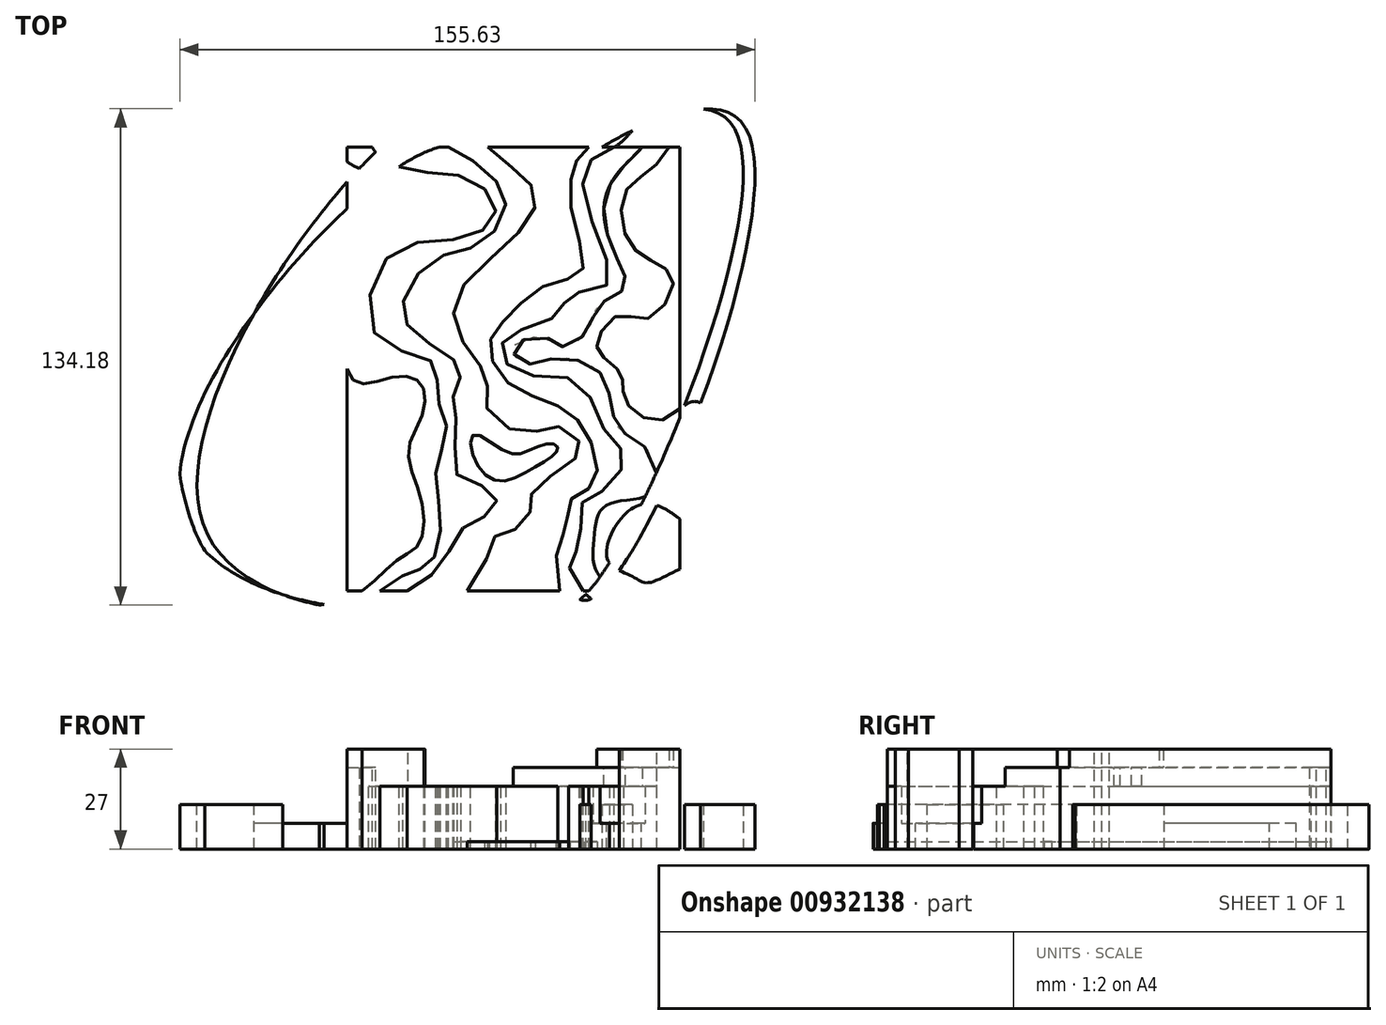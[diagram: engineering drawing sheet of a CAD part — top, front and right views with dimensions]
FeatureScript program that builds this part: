
annotation { "Feature Type Name" : "Feature", "Feature Type Description" : "" }
export const myFeature = defineFeature(function(context is Context, id is Id, definition is map)
    precondition{}
    {
        {
            var Q0;
            Q0=qCreatedBy(makeId("Top.planeOp"),FACE);
            var sketch = newSketch(context, id + "F0", { "sketchPlane" : qUnion([Q0])});
            skLineSegment(sketch, "E0.bottom", {"start": v(-45, 60) * mm, "end": v(-6.97, 60) * mm});
            skLineSegment(sketch, "E0.top", {"start": v(-45, -60) * mm, "end": v(-12.44, -60) * mm});
            skLineSegment(sketch, "E0.left", {"start": v(-45, 60) * mm, "end": v(-45, -60) * mm});
            skLineSegment(sketch, "E0.right", {"start": v(45, 60) * mm, "end": v(45, -60) * mm});
            skPoint(sketch, "E0.middle", {"position": v(0, 0) * mm});
            skLineSegment(sketch, "E1", {"start": v(-6.97, 60) * mm, "end": v(20.41, 60) * mm});
            skFitSpline(sketch, "E2", {"points": [v(16.04, -63.26) * mm, v(11.9, -48.78) * mm, v(14.27, -42.87) * mm, v(15.6, -35.28) * mm, v(21.8, -30.98) * mm, v(20.34, -18.36) * mm, v(12.06, -9.94) * mm, v(-1.19, -3.87) * mm, v(-6.45, 6.58) * mm, v(-1.58, 14) * mm, v(9.35, 22.97) * mm, v(18.56, 26.42) * mm, v(15.55, 43.43) * mm, v(16.67, 55.35) * mm, v(21.42, 60.68) * mm, v(59.74, 65.27) * mm, v(16.04, -63.26) * mm]});
            skLineSegment(sketch, "E3", {"start": v(-12.44, -60) * mm, "end": v(45, -60) * mm});
            skFitSpline(sketch, "E4", {"points": [v(-83.72, -42.55) * mm, v(-12.44, -60) * mm, v(-5.8, -46.06) * mm, v(0, -43.59) * mm, v(4.76, -37.85) * mm, v(5.15, -33.16) * mm, v(15.44, -25.35) * mm, v(18.05, -20.26) * mm, v(11.4, -15.44) * mm, v(3.2, -17.4) * mm, v(-7.36, -10.1) * mm, v(-6.97, -3.2) * mm, v(-12.18, 5.15) * mm, v(-15.96, 17.66) * mm, v(-3.97, 31.86) * mm, v(5.93, 44.1) * mm, v(3.32, 51.54) * mm, v(-6.97, 60) * mm, v(-20.78, 70.04) * mm, v(-83.72, -42.55) * mm]});
            skLineSegment(sketch, "E5", {"start": v(20.41, 60) * mm, "end": v(45, 60) * mm});
            skFitSpline(sketch, "E6", {"points": [v(-88.1, -42.66) * mm, v(-16.81, -60.11) * mm, v(-9.85, -43.73) * mm, v(-2, -41.73) * mm, v(1.36, -37.65) * mm, v(2.18, -31.48) * mm, v(12.7, -23.96) * mm, v(14.56, -20.06) * mm, v(10.66, -17.88) * mm, v(2.32, -19.65) * mm, v(-11.73, -10.21) * mm, v(-11.2, -3.5) * mm, v(-15.41, 3.57) * mm, v(-19.59, 18.67) * mm, v(-6.19, 33.06) * mm, v(0, 44.17) * mm, v(-4.9, 54.09) * mm, v(-11.34, 59.89) * mm, v(-34.22, 52.4) * mm, v(-88.1, -42.66) * mm]});
            skFitSpline(sketch, "E7", {"points": [v(20.42, -62.42) * mm, v(13.66, -51.71) * mm, v(16.56, -43.66) * mm, v(17, -36.27) * mm, v(23.02, -31.54) * mm, v(22.77, -17.31) * mm, v(14.52, -5.88) * mm, v(0.66, -2.03) * mm, v(-4.46, 6.31) * mm, v(0.4, 12.19) * mm, v(13.12, 21.41) * mm, v(22.39, 24) * mm, v(18.07, 43.72) * mm, v(18.51, 54.84) * mm, v(24.7, 60.46) * mm, v(62.73, 65.36) * mm, v(20.42, -62.42) * mm]});
            skPoint(sketch, "E8", {"position": v(16.28, -60) * mm});
            skFitSpline(sketch, "E9", {"points": [v(18.81, -60) * mm, v(15.05, -51.82) * mm, v(18.09, -47.5) * mm, v(18.23, -36.77) * mm, v(24.7, -32.5) * mm, v(29.92, -23.49) * mm, v(25.07, -17.13) * mm, v(17.26, -3.35) * mm, v(1.58, -1.12) * mm, v(-3.31, 5.95) * mm, v(1.86, 10.53) * mm, v(13.37, 15.93) * mm, v(14.55, 19.78) * mm, v(25.03, 22.5) * mm, v(22.83, 35.84) * mm, v(19.4, 54.52) * mm, v(27.3, 60) * mm, v(39.28, 72.86) * mm, v(84.63, 91.55) * mm, v(93.88, -78.95) * mm, v(29.67, -67.33) * mm, v(18.81, -60) * mm]});
            skFitSpline(sketch, "E10", {"points": [v(4.1, -22.01) * mm, v(10.22, -20.15) * mm, v(11.97, -21.26) * mm, v(10.98, -23.16) * mm, v(5.15, -26.94) * mm, v(-3.68, -30.33) * mm, v(-10.43, -24.68) * mm, v(-10.65, -17.74) * mm, v(-1.49, -22.63) * mm, v(4.1, -22.01) * mm]});
            skFitSpline(sketch, "E11", {"points": [v(-28.72, -60) * mm, v(-19.06, -52.14) * mm, v(-12.96, -42.38) * mm, v(-5.87, -38.64) * mm, v(-5.41, -33.16) * mm, v(-15.25, -28.65) * mm, v(-15.25, -16.07) * mm, v(-16.4, -8.37) * mm, v(-14.41, -2.12) * mm, v(-16.4, 2.69) * mm, v(-27.53, 10.54) * mm, v(-29.74, 18.55) * mm, v(-20.44, 30.14) * mm, v(-9.3, 33.65) * mm, v(-2.13, 44.1) * mm, v(-6.56, 52.8) * mm, v(-17.54, 60) * mm, v(-21.48, 61.98) * mm, v(-56.3, 96.44) * mm, v(-92.95, 76.5) * mm, v(-86.24, -79.13) * mm, v(-33.09, -76.78) * mm, v(-35.69, -65.14) * mm, v(-28.72, -60) * mm]});
            skFitSpline(sketch, "E12", {"points": [v(27.38, -60) * mm, v(22.04, -53.76) * mm, v(21.73, -46.29) * mm, v(23.1, -39.12) * mm, v(27.68, -35.91) * mm, v(37.75, -33.02) * mm, v(35.92, -21.58) * mm, v(28.6, -16.09) * mm, v(26.16, -7.85) * mm, v(22.34, 0) * mm, v(10.9, 2.83) * mm, v(3.28, 1.46) * mm, v(0, 5.73) * mm, v(8.47, 8.62) * mm, v(13.04, 6.03) * mm, v(20.2, 10.6) * mm, v(23.26, 17.32) * mm, v(29.06, 20.83) * mm, v(30.28, 24.64) * mm, v(27.53, 31.04) * mm, v(24.48, 42.48) * mm, v(27.68, 52.4) * mm, v(34.85, 60) * mm, v(45.83, 74.67) * mm, v(63.98, 87.02) * mm, v(86.1, 85.5) * mm, v(99.67, -46.29) * mm, v(87.63, -77.25) * mm, v(44.46, -72.06) * mm, v(27.38, -60) * mm]});
            skFitSpline(sketch, "E13", {"points": [v(-36.07, -60) * mm, v(-27.38, -54.83) * mm, v(-22.2, -52.08) * mm, v(-19.75, -39.57) * mm, v(-20.82, -26.3) * mm, v(-18.07, -16.09) * mm, v(-20.67, -7.09) * mm, v(-21.58, 1.6) * mm, v(-36.83, 8.62) * mm, v(-33.02, 31.2) * mm, v(-12.58, 35.62) * mm, v(-4.8, 42.94) * mm, v(-12.58, 51.64) * mm, v(-28.6, 53.92) * mm, v(-36.38, 58.04) * mm, v(-38.2, 60) * mm, v(-54.07, 85.5) * mm, v(-88.08, 71) * mm, v(-98.45, -46.13) * mm, v(-69.48, -80.45) * mm, v(-36.07, -60) * mm]});
            skFitSpline(sketch, "E14", {"points": [v(47.82, 67.2) * mm, v(37.75, 54.38) * mm, v(30.12, 47.67) * mm, v(31.2, 34.25) * mm, v(38.2, 28.9) * mm, v(43.24, 23.57) * mm, v(36.22, 13.66) * mm, v(28.6, 14.57) * mm, v(22.65, 7.56) * mm, v(24.02, 3.6) * mm, v(29.2, -1.3) * mm, v(29.51, -4.65) * mm, v(31.5, -10.29) * mm, v(40.04, -13.8) * mm, v(48.88, -8.76) * mm, v(56.82, -21.42) * mm, v(53.92, -45.22) * mm, v(42.63, -38.81) * mm, v(31.8, -37.9) * mm, v(25.4, -51.32) * mm, v(32.1, -56.05) * mm, v(36.99, -57.72) * mm, v(48.73, -53.76) * mm, v(62.15, -69.62) * mm, v(81.37, -74.04) * mm, v(91.44, -26) * mm, v(91.74, 45.08) * mm, v(79.39, 80.16) * mm, v(47.82, 67.2) * mm]});
            skFitSpline(sketch, "E15", {"points": [v(-59.26, 80.46) * mm, v(-48.43, 60) * mm, v(-37.14, 52.7) * mm, v(-24.02, 49.8) * mm, v(-17.62, 49.8) * mm, v(-13.2, 47.52) * mm, v(-12.13, 39.28) * mm, v(-18.23, 37.6) * mm, v(-23.08, 39.3) * mm, v(-37.57, 39.46) * mm, v(-42.82, 33.17) * mm, v(-46.64, 25.05) * mm, v(-46.24, 6.74) * mm, v(-42.33, -3.73) * mm, v(-32.31, -2.18) * mm, v(-25.24, -3.73) * mm, v(-24.48, -11.66) * mm, v(-28.45, -22.34) * mm, v(-24.94, -35.46) * mm, v(-25.7, -47.5) * mm, v(-31.65, -51.78) * mm, v(-40.95, -60) * mm, v(-57.73, -63.83) * mm, v(-81.22, -52.39) * mm, v(-92.2, -8.76) * mm, v(-83.81, 51.79) * mm, v(-59.26, 80.46) * mm]});
            skSolve(sketch);
        }
        {
            var Q0;
            {var subQ0=sQuery(id+"F0.wireOp",EDGE,"E0.left");var subQ1=sQuery(id+"F0.wireOp",EDGE,"E0.top");var subQ2=makeQuery(id+"F0.imprint","INTERSECT",VERTEX,{"derivedFrom":[subQ1,subQ0]});Q0=makeQuery(id+"F0.imprint","IMPRINT",FACE,{"disambiguationData":[TD([[makeQuery(id+"F0.imprint","IMPRINT",EDGE,{"disambiguationData":[TD([[subQ2,-1.0]])],"derivedFrom":subQ1}),1.0]])]});}
            var Q1;
            {var subQ1=sQuery(id+"F0.wireOp",EDGE,"E0.bottom");var subQ5=sQuery(id+"F0.wireOp",EDGE,"E0.left");var subQ6=makeQuery(id+"F0.imprint","INTERSECT",VERTEX,{"derivedFrom":[subQ1,subQ5]});Q1=makeQuery(id+"F0.imprint","IMPRINT",FACE,{"disambiguationData":[TD([[makeQuery(id+"F0.imprint","IMPRINT",EDGE,{"disambiguationData":[TD([[subQ6,-1.0]])],"derivedFrom":subQ1}),-1.0]])]});}
            var Q2;
            {var subQ0=sQuery(id+"F0.wireOp",EDGE,"E11");var subQ1=sQuery(id+"F0.wireOp",EDGE,"E0.bottom");var subQ2=makeQuery(id+"F0.imprint","INTERSECT",VERTEX,{"derivedFrom":[subQ1,subQ0]});Q2=makeQuery(id+"F0.imprint","IMPRINT",FACE,{"disambiguationData":[TD([[makeQuery(id+"F0.imprint","IMPRINT",EDGE,{"disambiguationData":[TD([[subQ2,1.0]])],"derivedFrom":subQ1}),-1.0]])]});}
            var Q3;
            {var subQ0=sQuery(id+"F0.wireOp",EDGE,"E6");Q3=makeQuery(id+"F0.imprint","IMPRINT",FACE,{"disambiguationData":[TD([[makeQuery(id+"F0.imprint","IMPRINT",EDGE,{"derivedFrom":subQ0}),1.0]])]});}
            var Q4;
            {var subQ0=sQuery(id+"F0.wireOp",EDGE,"E4");Q4=makeQuery(id+"F0.imprint","IMPRINT",FACE,{"disambiguationData":[TD([[makeQuery(id+"F0.imprint","IMPRINT",EDGE,{"derivedFrom":subQ0}),1.0]])]});}
            var Q5;
            Q5=makeQuery(id+"F0.imprint","IMPRINT",FACE,{"disambiguationData":[TD([[makeQuery(id+"F0.imprint","IMPRINT",EDGE,{"derivedFrom":sQuery(id+"F0.wireOp",EDGE,"E1")}),-1.0]])]});
            var Q6;
            {var subQ0=sQuery(id+"F0.wireOp",EDGE,"E2");Q6=makeQuery(id+"F0.imprint","IMPRINT",FACE,{"disambiguationData":[TD([[makeQuery(id+"F0.imprint","IMPRINT",EDGE,{"derivedFrom":subQ0}),-1.0]])]});}
            var Q7;
            {var subQ0=sQuery(id+"F0.wireOp",EDGE,"E7");Q7=makeQuery(id+"F0.imprint","IMPRINT",FACE,{"disambiguationData":[TD([[makeQuery(id+"F0.imprint","IMPRINT",EDGE,{"derivedFrom":subQ0}),-1.0]])]});}
            var Q8;
            {var subQ0=sQuery(id+"F0.wireOp",EDGE,"E9");var subQ1=sQuery(id+"F0.wireOp",EDGE,"E3");var subQ2=makeQuery(id+"F0.imprint","INTERSECT",VERTEX,{"derivedFrom":[subQ1,subQ0]});Q8=makeQuery(id+"F0.imprint","IMPRINT",FACE,{"disambiguationData":[TD([[makeQuery(id+"F0.imprint","IMPRINT",EDGE,{"disambiguationData":[TD([[subQ2,-1.0]])],"derivedFrom":subQ1}),1.0]])]});}
            var Q9;
            {var subQ3=sQuery(id+"F0.wireOp",EDGE,"E14");var subQ6=sQuery(id+"F0.wireOp",EDGE,"E0.right");var subQ9=makeQuery(id+"F0.imprint","INTERSECT",VERTEX,{"disambiguationData":[OD(0.0)],"derivedFrom":[subQ6,subQ3]});Q9=makeQuery(id+"F0.imprint","IMPRINT",FACE,{"disambiguationData":[TD([[makeQuery(id+"F0.imprint","IMPRINT",EDGE,{"disambiguationData":[TD([[subQ9,-1.0]])],"derivedFrom":subQ6}),-1.0]])]});}
            var Q10;
            {var subQ0=sQuery(id+"F0.wireOp",EDGE,"E5");var subQ1=sQuery(id+"F0.wireOp",EDGE,"E0.right");var subQ2=makeQuery(id+"F0.imprint","INTERSECT",VERTEX,{"derivedFrom":[subQ1,subQ0]});Q10=makeQuery(id+"F0.imprint","IMPRINT",FACE,{"disambiguationData":[TD([[makeQuery(id+"F0.imprint","IMPRINT",EDGE,{"disambiguationData":[TD([[subQ2,-1.0]])],"derivedFrom":subQ1}),-1.0]])]});}
            var Q11;
            {var subQ0=sQuery(id+"F0.wireOp",EDGE,"E14");var subQ1=sQuery(id+"F0.wireOp",EDGE,"E0.right");var subQ2=makeQuery(id+"F0.imprint","INTERSECT",VERTEX,{"disambiguationData":[OD(1.0)],"derivedFrom":[subQ1,subQ0]});Q11=makeQuery(id+"F0.imprint","IMPRINT",FACE,{"disambiguationData":[TD([[makeQuery(id+"F0.imprint","IMPRINT",EDGE,{"disambiguationData":[TD([[subQ2,-1.0]])],"derivedFrom":subQ1}),-1.0]])]});}
            var Q12;
            Q12=makeQuery(id+"F0.imprint","IMPRINT",FACE,{"disambiguationData":[TD([[makeQuery(id+"F0.imprint","IMPRINT",EDGE,{"derivedFrom":sQuery(id+"F0.wireOp",EDGE,"E10")}),-1.0]])]});
            var Q13;
            {var subQ0=sQuery(id+"F0.wireOp",EDGE,"E15");var subQ1=sQuery(id+"F0.wireOp",EDGE,"E0.left");var subQ2=makeQuery(id+"F0.imprint","INTERSECT",VERTEX,{"disambiguationData":[OD(0.0)],"derivedFrom":[subQ1,subQ0]});Q13=makeQuery(id+"F0.imprint","IMPRINT",FACE,{"disambiguationData":[TD([[makeQuery(id+"F0.imprint","IMPRINT",EDGE,{"disambiguationData":[TD([[subQ2,-1.0]])],"derivedFrom":subQ1}),1.0]])]});}
            extrude(context, id + "F1", {"entities" : qUnion([Q0, Q1, Q2, Q3, Q4, Q5, Q6, Q7, Q8, Q9, Q10, Q11, Q12, Q13]), "oppositeDirection" : true, "depth" : 2 * mm, "offsetDistance" : 25 * mm});
        }
        {
            var Q0;
            {var subQ0=sQuery(id+"F0.wireOp",EDGE,"E4");Q0=makeQuery(id+"F0.imprint","IMPRINT",FACE,{"disambiguationData":[TD([[makeQuery(id+"F0.imprint","IMPRINT",EDGE,{"derivedFrom":subQ0}),1.0]])]});}
            var Q1;
            {var subQ0=sQuery(id+"F0.wireOp",EDGE,"E2");Q1=makeQuery(id+"F0.imprint","IMPRINT",FACE,{"disambiguationData":[TD([[makeQuery(id+"F0.imprint","IMPRINT",EDGE,{"derivedFrom":subQ0}),-1.0]])]});}
            var Q2;
            {var subQ0=sQuery(id+"F0.wireOp",EDGE,"E7");Q2=makeQuery(id+"F0.imprint","IMPRINT",FACE,{"disambiguationData":[TD([[makeQuery(id+"F0.imprint","IMPRINT",EDGE,{"derivedFrom":subQ0}),-1.0]])]});}
            var Q3;
            {var subQ0=sQuery(id+"F0.wireOp",EDGE,"E9");var subQ1=sQuery(id+"F0.wireOp",EDGE,"E3");var subQ2=makeQuery(id+"F0.imprint","INTERSECT",VERTEX,{"derivedFrom":[subQ1,subQ0]});Q3=makeQuery(id+"F0.imprint","IMPRINT",FACE,{"disambiguationData":[TD([[makeQuery(id+"F0.imprint","IMPRINT",EDGE,{"disambiguationData":[TD([[subQ2,-1.0]])],"derivedFrom":subQ1}),1.0]])]});}
            var Q4;
            {var subQ3=sQuery(id+"F0.wireOp",EDGE,"E14");var subQ6=sQuery(id+"F0.wireOp",EDGE,"E0.right");var subQ10=makeQuery(id+"F0.imprint","INTERSECT",VERTEX,{"disambiguationData":[OD(0.0)],"derivedFrom":[subQ6,subQ3]});Q4=makeQuery(id+"F0.imprint","IMPRINT",FACE,{"disambiguationData":[TD([[makeQuery(id+"F0.imprint","IMPRINT",EDGE,{"disambiguationData":[TD([[subQ10,-1.0]])],"derivedFrom":subQ6}),-1.0]])]});}
            var Q5;
            {var subQ0=sQuery(id+"F0.wireOp",EDGE,"E5");var subQ1=sQuery(id+"F0.wireOp",EDGE,"E0.right");var subQ2=makeQuery(id+"F0.imprint","INTERSECT",VERTEX,{"derivedFrom":[subQ1,subQ0]});Q5=makeQuery(id+"F0.imprint","IMPRINT",FACE,{"disambiguationData":[TD([[makeQuery(id+"F0.imprint","IMPRINT",EDGE,{"disambiguationData":[TD([[subQ2,-1.0]])],"derivedFrom":subQ1}),-1.0]])]});}
            var Q6;
            {var subQ0=sQuery(id+"F0.wireOp",EDGE,"E14");var subQ1=sQuery(id+"F0.wireOp",EDGE,"E0.right");var subQ2=makeQuery(id+"F0.imprint","INTERSECT",VERTEX,{"disambiguationData":[OD(1.0)],"derivedFrom":[subQ1,subQ0]});Q6=makeQuery(id+"F0.imprint","IMPRINT",FACE,{"disambiguationData":[TD([[makeQuery(id+"F0.imprint","IMPRINT",EDGE,{"disambiguationData":[TD([[subQ2,-1.0]])],"derivedFrom":subQ1}),-1.0]])]});}
            var Q7;
            {var subQ0=sQuery(id+"F0.wireOp",EDGE,"E6");Q7=makeQuery(id+"F0.imprint","IMPRINT",FACE,{"disambiguationData":[TD([[makeQuery(id+"F0.imprint","IMPRINT",EDGE,{"derivedFrom":subQ0}),1.0]])]});}
            var Q8;
            {var subQ0=sQuery(id+"F0.wireOp",EDGE,"E11");var subQ1=sQuery(id+"F0.wireOp",EDGE,"E0.bottom");var subQ2=makeQuery(id+"F0.imprint","INTERSECT",VERTEX,{"derivedFrom":[subQ1,subQ0]});Q8=makeQuery(id+"F0.imprint","IMPRINT",FACE,{"disambiguationData":[TD([[makeQuery(id+"F0.imprint","IMPRINT",EDGE,{"disambiguationData":[TD([[subQ2,1.0]])],"derivedFrom":subQ1}),-1.0]])]});}
            var Q9;
            {var subQ1=sQuery(id+"F0.wireOp",EDGE,"E0.bottom");var subQ5=sQuery(id+"F0.wireOp",EDGE,"E0.left");var subQ6=makeQuery(id+"F0.imprint","INTERSECT",VERTEX,{"derivedFrom":[subQ1,subQ5]});Q9=makeQuery(id+"F0.imprint","IMPRINT",FACE,{"disambiguationData":[TD([[makeQuery(id+"F0.imprint","IMPRINT",EDGE,{"disambiguationData":[TD([[subQ6,-1.0]])],"derivedFrom":subQ1}),-1.0]])]});}
            var Q10;
            {var subQ0=sQuery(id+"F0.wireOp",EDGE,"E0.left");var subQ1=sQuery(id+"F0.wireOp",EDGE,"E0.top");var subQ2=makeQuery(id+"F0.imprint","INTERSECT",VERTEX,{"derivedFrom":[subQ1,subQ0]});Q10=makeQuery(id+"F0.imprint","IMPRINT",FACE,{"disambiguationData":[TD([[makeQuery(id+"F0.imprint","IMPRINT",EDGE,{"disambiguationData":[TD([[subQ2,-1.0]])],"derivedFrom":subQ1}),1.0]])]});}
            var Q11;
            Q11=makeQuery(id+"F0.imprint","IMPRINT",FACE,{"disambiguationData":[TD([[makeQuery(id+"F0.imprint","IMPRINT",EDGE,{"derivedFrom":sQuery(id+"F0.wireOp",EDGE,"E10")}),-1.0]])]});
            extrude(context, id + "F2", {"entities" : qUnion([Q0, Q1, Q2, Q3, Q4, Q5, Q6, Q7, Q8, Q9, Q10, Q11]), "operationType" : NewBodyOperationType.ADD, "depth" : (5 * 1) * mm, "offsetDistance" : 25 * mm});
        }
        {
            var Q0;
            {var subQ0=sQuery(id+"F0.wireOp",EDGE,"E7");Q0=makeQuery(id+"F0.imprint","IMPRINT",FACE,{"disambiguationData":[TD([[makeQuery(id+"F0.imprint","IMPRINT",EDGE,{"derivedFrom":subQ0}),-1.0]])]});}
            var Q1;
            {var subQ0=sQuery(id+"F0.wireOp",EDGE,"E9");var subQ1=sQuery(id+"F0.wireOp",EDGE,"E3");var subQ2=makeQuery(id+"F0.imprint","INTERSECT",VERTEX,{"derivedFrom":[subQ1,subQ0]});Q1=makeQuery(id+"F0.imprint","IMPRINT",FACE,{"disambiguationData":[TD([[makeQuery(id+"F0.imprint","IMPRINT",EDGE,{"disambiguationData":[TD([[subQ2,-1.0]])],"derivedFrom":subQ1}),1.0]])]});}
            var Q2;
            {var subQ3=sQuery(id+"F0.wireOp",EDGE,"E14");var subQ6=sQuery(id+"F0.wireOp",EDGE,"E0.right");var subQ10=makeQuery(id+"F0.imprint","INTERSECT",VERTEX,{"disambiguationData":[OD(0.0)],"derivedFrom":[subQ6,subQ3]});Q2=makeQuery(id+"F0.imprint","IMPRINT",FACE,{"disambiguationData":[TD([[makeQuery(id+"F0.imprint","IMPRINT",EDGE,{"disambiguationData":[TD([[subQ10,-1.0]])],"derivedFrom":subQ6}),-1.0]])]});}
            var Q3;
            {var subQ0=sQuery(id+"F0.wireOp",EDGE,"E5");var subQ1=sQuery(id+"F0.wireOp",EDGE,"E0.right");var subQ2=makeQuery(id+"F0.imprint","INTERSECT",VERTEX,{"derivedFrom":[subQ1,subQ0]});Q3=makeQuery(id+"F0.imprint","IMPRINT",FACE,{"disambiguationData":[TD([[makeQuery(id+"F0.imprint","IMPRINT",EDGE,{"disambiguationData":[TD([[subQ2,-1.0]])],"derivedFrom":subQ1}),-1.0]])]});}
            var Q4;
            {var subQ0=sQuery(id+"F0.wireOp",EDGE,"E14");var subQ1=sQuery(id+"F0.wireOp",EDGE,"E0.right");var subQ2=makeQuery(id+"F0.imprint","INTERSECT",VERTEX,{"disambiguationData":[OD(1.0)],"derivedFrom":[subQ1,subQ0]});Q4=makeQuery(id+"F0.imprint","IMPRINT",FACE,{"disambiguationData":[TD([[makeQuery(id+"F0.imprint","IMPRINT",EDGE,{"disambiguationData":[TD([[subQ2,-1.0]])],"derivedFrom":subQ1}),-1.0]])]});}
            var Q5;
            {var subQ0=sQuery(id+"F0.wireOp",EDGE,"E6");Q5=makeQuery(id+"F0.imprint","IMPRINT",FACE,{"disambiguationData":[TD([[makeQuery(id+"F0.imprint","IMPRINT",EDGE,{"derivedFrom":subQ0}),1.0]])]});}
            var Q6;
            {var subQ0=sQuery(id+"F0.wireOp",EDGE,"E11");var subQ1=sQuery(id+"F0.wireOp",EDGE,"E0.bottom");var subQ2=makeQuery(id+"F0.imprint","INTERSECT",VERTEX,{"derivedFrom":[subQ1,subQ0]});Q6=makeQuery(id+"F0.imprint","IMPRINT",FACE,{"disambiguationData":[TD([[makeQuery(id+"F0.imprint","IMPRINT",EDGE,{"disambiguationData":[TD([[subQ2,1.0]])],"derivedFrom":subQ1}),-1.0]])]});}
            var Q7;
            {var subQ1=sQuery(id+"F0.wireOp",EDGE,"E0.bottom");var subQ5=sQuery(id+"F0.wireOp",EDGE,"E0.left");var subQ6=makeQuery(id+"F0.imprint","INTERSECT",VERTEX,{"derivedFrom":[subQ1,subQ5]});Q7=makeQuery(id+"F0.imprint","IMPRINT",FACE,{"disambiguationData":[TD([[makeQuery(id+"F0.imprint","IMPRINT",EDGE,{"disambiguationData":[TD([[subQ6,-1.0]])],"derivedFrom":subQ1}),-1.0]])]});}
            var Q8;
            {var subQ0=sQuery(id+"F0.wireOp",EDGE,"E0.left");var subQ1=sQuery(id+"F0.wireOp",EDGE,"E0.top");var subQ2=makeQuery(id+"F0.imprint","INTERSECT",VERTEX,{"derivedFrom":[subQ1,subQ0]});Q8=makeQuery(id+"F0.imprint","IMPRINT",FACE,{"disambiguationData":[TD([[makeQuery(id+"F0.imprint","IMPRINT",EDGE,{"disambiguationData":[TD([[subQ2,-1.0]])],"derivedFrom":subQ1}),1.0]])]});}
            var Q9;
            Q9=makeQuery(id+"F0.imprint","IMPRINT",FACE,{"disambiguationData":[TD([[makeQuery(id+"F0.imprint","IMPRINT",EDGE,{"derivedFrom":sQuery(id+"F0.wireOp",EDGE,"E10")}),-1.0]])]});
            extrude(context, id + "F3", {"entities" : qUnion([Q0, Q1, Q2, Q3, Q4, Q5, Q6, Q7, Q8, Q9]), "operationType" : NewBodyOperationType.ADD, "depth" : (5 * 2) * mm, "offsetDistance" : 25 * mm});
        }
        {
            var Q0;
            {var subQ0=sQuery(id+"F0.wireOp",EDGE,"E11");var subQ1=sQuery(id+"F0.wireOp",EDGE,"E0.bottom");var subQ2=makeQuery(id+"F0.imprint","INTERSECT",VERTEX,{"derivedFrom":[subQ1,subQ0]});Q0=makeQuery(id+"F0.imprint","IMPRINT",FACE,{"disambiguationData":[TD([[makeQuery(id+"F0.imprint","IMPRINT",EDGE,{"disambiguationData":[TD([[subQ2,1.0]])],"derivedFrom":subQ1}),-1.0]])]});}
            var Q1;
            {var subQ0=sQuery(id+"F0.wireOp",EDGE,"E9");var subQ1=sQuery(id+"F0.wireOp",EDGE,"E3");var subQ2=makeQuery(id+"F0.imprint","INTERSECT",VERTEX,{"derivedFrom":[subQ1,subQ0]});Q1=makeQuery(id+"F0.imprint","IMPRINT",FACE,{"disambiguationData":[TD([[makeQuery(id+"F0.imprint","IMPRINT",EDGE,{"disambiguationData":[TD([[subQ2,-1.0]])],"derivedFrom":subQ1}),1.0]])]});}
            var Q2;
            {var subQ3=sQuery(id+"F0.wireOp",EDGE,"E14");var subQ6=sQuery(id+"F0.wireOp",EDGE,"E0.right");var subQ10=makeQuery(id+"F0.imprint","INTERSECT",VERTEX,{"disambiguationData":[OD(0.0)],"derivedFrom":[subQ6,subQ3]});Q2=makeQuery(id+"F0.imprint","IMPRINT",FACE,{"disambiguationData":[TD([[makeQuery(id+"F0.imprint","IMPRINT",EDGE,{"disambiguationData":[TD([[subQ10,-1.0]])],"derivedFrom":subQ6}),-1.0]])]});}
            var Q3;
            {var subQ0=sQuery(id+"F0.wireOp",EDGE,"E5");var subQ1=sQuery(id+"F0.wireOp",EDGE,"E0.right");var subQ2=makeQuery(id+"F0.imprint","INTERSECT",VERTEX,{"derivedFrom":[subQ1,subQ0]});Q3=makeQuery(id+"F0.imprint","IMPRINT",FACE,{"disambiguationData":[TD([[makeQuery(id+"F0.imprint","IMPRINT",EDGE,{"disambiguationData":[TD([[subQ2,-1.0]])],"derivedFrom":subQ1}),-1.0]])]});}
            var Q4;
            {var subQ0=sQuery(id+"F0.wireOp",EDGE,"E14");var subQ1=sQuery(id+"F0.wireOp",EDGE,"E0.right");var subQ2=makeQuery(id+"F0.imprint","INTERSECT",VERTEX,{"disambiguationData":[OD(1.0)],"derivedFrom":[subQ1,subQ0]});Q4=makeQuery(id+"F0.imprint","IMPRINT",FACE,{"disambiguationData":[TD([[makeQuery(id+"F0.imprint","IMPRINT",EDGE,{"disambiguationData":[TD([[subQ2,-1.0]])],"derivedFrom":subQ1}),-1.0]])]});}
            var Q5;
            Q5=makeQuery(id+"F0.imprint","IMPRINT",FACE,{"disambiguationData":[TD([[makeQuery(id+"F0.imprint","IMPRINT",EDGE,{"derivedFrom":sQuery(id+"F0.wireOp",EDGE,"E10")}),-1.0]])]});
            var Q6;
            {var subQ1=sQuery(id+"F0.wireOp",EDGE,"E0.bottom");var subQ5=sQuery(id+"F0.wireOp",EDGE,"E0.left");var subQ6=makeQuery(id+"F0.imprint","INTERSECT",VERTEX,{"derivedFrom":[subQ1,subQ5]});Q6=makeQuery(id+"F0.imprint","IMPRINT",FACE,{"disambiguationData":[TD([[makeQuery(id+"F0.imprint","IMPRINT",EDGE,{"disambiguationData":[TD([[subQ6,-1.0]])],"derivedFrom":subQ1}),-1.0]])]});}
            var Q7;
            {var subQ0=sQuery(id+"F0.wireOp",EDGE,"E0.left");var subQ1=sQuery(id+"F0.wireOp",EDGE,"E0.top");var subQ2=makeQuery(id+"F0.imprint","INTERSECT",VERTEX,{"derivedFrom":[subQ1,subQ0]});Q7=makeQuery(id+"F0.imprint","IMPRINT",FACE,{"disambiguationData":[TD([[makeQuery(id+"F0.imprint","IMPRINT",EDGE,{"disambiguationData":[TD([[subQ2,-1.0]])],"derivedFrom":subQ1}),1.0]])]});}
            extrude(context, id + "F4", {"entities" : qUnion([Q0, Q1, Q2, Q3, Q4, Q5, Q6, Q7]), "operationType" : NewBodyOperationType.ADD, "depth" : (5 * 3) * mm, "offsetDistance" : 25 * mm});
        }
        {
            var Q0;
            {var subQ1=sQuery(id+"F0.wireOp",EDGE,"E0.bottom");var subQ5=sQuery(id+"F0.wireOp",EDGE,"E0.left");var subQ6=makeQuery(id+"F0.imprint","INTERSECT",VERTEX,{"derivedFrom":[subQ1,subQ5]});Q0=makeQuery(id+"F0.imprint","IMPRINT",FACE,{"disambiguationData":[TD([[makeQuery(id+"F0.imprint","IMPRINT",EDGE,{"disambiguationData":[TD([[subQ6,-1.0]])],"derivedFrom":subQ1}),-1.0]])]});}
            var Q1;
            {var subQ0=sQuery(id+"F0.wireOp",EDGE,"E0.left");var subQ1=sQuery(id+"F0.wireOp",EDGE,"E0.top");var subQ2=makeQuery(id+"F0.imprint","INTERSECT",VERTEX,{"derivedFrom":[subQ1,subQ0]});Q1=makeQuery(id+"F0.imprint","IMPRINT",FACE,{"disambiguationData":[TD([[makeQuery(id+"F0.imprint","IMPRINT",EDGE,{"disambiguationData":[TD([[subQ2,-1.0]])],"derivedFrom":subQ1}),1.0]])]});}
            var Q2;
            {var subQ3=sQuery(id+"F0.wireOp",EDGE,"E14");var subQ6=sQuery(id+"F0.wireOp",EDGE,"E0.right");var subQ10=makeQuery(id+"F0.imprint","INTERSECT",VERTEX,{"disambiguationData":[OD(0.0)],"derivedFrom":[subQ6,subQ3]});Q2=makeQuery(id+"F0.imprint","IMPRINT",FACE,{"disambiguationData":[TD([[makeQuery(id+"F0.imprint","IMPRINT",EDGE,{"disambiguationData":[TD([[subQ10,-1.0]])],"derivedFrom":subQ6}),-1.0]])]});}
            var Q3;
            {var subQ0=sQuery(id+"F0.wireOp",EDGE,"E5");var subQ1=sQuery(id+"F0.wireOp",EDGE,"E0.right");var subQ2=makeQuery(id+"F0.imprint","INTERSECT",VERTEX,{"derivedFrom":[subQ1,subQ0]});Q3=makeQuery(id+"F0.imprint","IMPRINT",FACE,{"disambiguationData":[TD([[makeQuery(id+"F0.imprint","IMPRINT",EDGE,{"disambiguationData":[TD([[subQ2,-1.0]])],"derivedFrom":subQ1}),-1.0]])]});}
            var Q4;
            {var subQ0=sQuery(id+"F0.wireOp",EDGE,"E14");var subQ1=sQuery(id+"F0.wireOp",EDGE,"E0.right");var subQ2=makeQuery(id+"F0.imprint","INTERSECT",VERTEX,{"disambiguationData":[OD(1.0)],"derivedFrom":[subQ1,subQ0]});Q4=makeQuery(id+"F0.imprint","IMPRINT",FACE,{"disambiguationData":[TD([[makeQuery(id+"F0.imprint","IMPRINT",EDGE,{"disambiguationData":[TD([[subQ2,-1.0]])],"derivedFrom":subQ1}),-1.0]])]});}
            extrude(context, id + "F5", {"entities" : qUnion([Q0, Q1, Q2, Q3, Q4]), "operationType" : NewBodyOperationType.ADD, "depth" : (5 * 4) * mm, "offsetDistance" : 25 * mm});
        }
        {
            var Q0;
            {var subQ0=sQuery(id+"F0.wireOp",EDGE,"E0.left");var subQ1=sQuery(id+"F0.wireOp",EDGE,"E0.top");var subQ2=makeQuery(id+"F0.imprint","INTERSECT",VERTEX,{"derivedFrom":[subQ1,subQ0]});Q0=makeQuery(id+"F0.imprint","IMPRINT",FACE,{"disambiguationData":[TD([[makeQuery(id+"F0.imprint","IMPRINT",EDGE,{"disambiguationData":[TD([[subQ2,-1.0]])],"derivedFrom":subQ1}),1.0]])]});}
            var Q1;
            {var subQ0=sQuery(id+"F0.wireOp",EDGE,"E5");var subQ1=sQuery(id+"F0.wireOp",EDGE,"E0.right");var subQ2=makeQuery(id+"F0.imprint","INTERSECT",VERTEX,{"derivedFrom":[subQ1,subQ0]});Q1=makeQuery(id+"F0.imprint","IMPRINT",FACE,{"disambiguationData":[TD([[makeQuery(id+"F0.imprint","IMPRINT",EDGE,{"disambiguationData":[TD([[subQ2,-1.0]])],"derivedFrom":subQ1}),-1.0]])]});}
            var Q2;
            {var subQ0=sQuery(id+"F0.wireOp",EDGE,"E14");var subQ1=sQuery(id+"F0.wireOp",EDGE,"E0.right");var subQ2=makeQuery(id+"F0.imprint","INTERSECT",VERTEX,{"disambiguationData":[OD(1.0)],"derivedFrom":[subQ1,subQ0]});Q2=makeQuery(id+"F0.imprint","IMPRINT",FACE,{"disambiguationData":[TD([[makeQuery(id+"F0.imprint","IMPRINT",EDGE,{"disambiguationData":[TD([[subQ2,-1.0]])],"derivedFrom":subQ1}),-1.0]])]});}
            var Q3;
            {var subQ0=sQuery(id+"F0.wireOp",EDGE,"E15");var subQ1=sQuery(id+"F0.wireOp",EDGE,"E0.left");var subQ2=makeQuery(id+"F0.imprint","INTERSECT",VERTEX,{"disambiguationData":[OD(0.0)],"derivedFrom":[subQ1,subQ0]});Q3=makeQuery(id+"F0.imprint","IMPRINT",FACE,{"disambiguationData":[TD([[makeQuery(id+"F0.imprint","IMPRINT",EDGE,{"disambiguationData":[TD([[subQ2,-1.0]])],"derivedFrom":subQ1}),1.0]])]});}
            extrude(context, id + "F6", {"entities" : qUnion([Q0, Q1, Q2, Q3]), "operationType" : NewBodyOperationType.ADD, "depth" : (5 * 5) * mm, "offsetDistance" : 25 * mm});
        }
    });
